SOLIDWORKS PART (.sldprt)
format: sldprt  version: not decoded by parser v0  size: 309,248 bytes
history: native  units: mm
features: plane x5, sketch x3, extrude x3, material x1, mirror x1 (+8 scaffold rows collapsed)
feature tree (21):
  scaffold x8  (default folders/planes/origin — collapsed)
  material  "Duranickel(R) 301"
  plane  "Alzado"
  plane  "Planta"
  plane  "Vista lateral"
  sketch  "Croquis1"  dims[c1.D4=4.0mm c1.D8=0.45mm c1.D11=2.0mm c1.D1=67.7mm c1.D2=31.8mm c1.D3=33.85mm c1.D5=11.5mm c2.D3=15.0mm c2.D6=1.0mm c2.D7=4.0mm c2.D9=2.0mm c2.D10=6.0mm]
  extrude  "Extruir1"  Depth=1mm
  sketch  "Croquis2"  dims[D1=10.0mm D2=22.5mm D3=2.5mm D4=2.0mm]
  extrude  "Extruir2"  Depth=1mm
  plane  "Plano1"  Offset=0.5mm
  sketch  "Croquis3"
  extrude  "Extruir3"  Depth=21.5mm
  plane  "Plano2"  Offset=0.5mm
  mirror  "Simetría2"
decode coverage: 5 of 7 modeling features carry decoded parameters
note: suppression state not decoded; provenance and decode notes live in map.json
